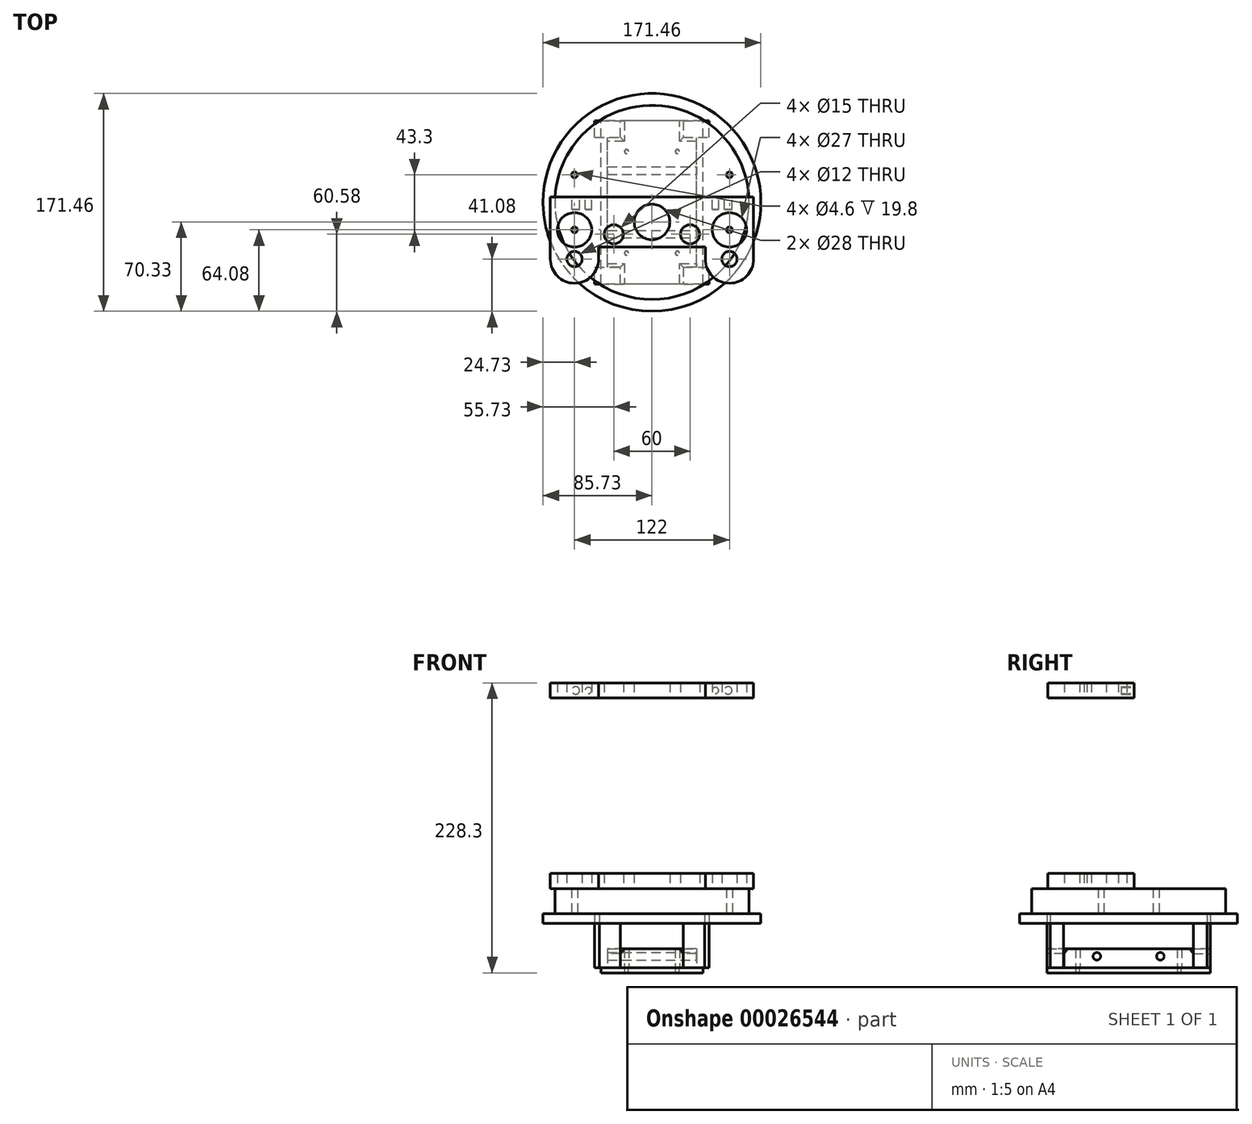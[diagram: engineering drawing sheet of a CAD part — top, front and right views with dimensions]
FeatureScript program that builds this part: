
annotation { "Feature Type Name" : "Feature", "Feature Type Description" : "" }
export const myFeature = defineFeature(function(context is Context, id is Id, definition is map)
    precondition{}
    {
        {
            var Q0;
            Q0=qCreatedBy(makeId("Top.planeOp"),FACE);
            var sketch = newSketch(context, id + "F0", { "sketchPlane" : qUnion([Q0])});
            skCircle(sketch, "E0", {"center": v(0, 0) * mm, "radius": 76.41 * mm});
            skCircle(sketch, "E1", {"center": v(-61, 21.65) * mm, "radius": 2.3 * mm});
            skCircle(sketch, "E2.0.1.0", {"center": v(-61, -21.65) * mm, "radius": 2.3 * mm});
            skCircle(sketch, "E2.1.0.0", {"center": v(61, 21.65) * mm, "radius": 2.3 * mm});
            skCircle(sketch, "E2.1.1.0", {"center": v(61, -21.65) * mm, "radius": 2.3 * mm});
            skLineSegment(sketch, "E2.direction2", {"start": v(-61, 21.65) * mm, "end": v(-61, -21.65) * mm, "construction": true});
            skSolve(sketch);
        }
        {
            var Q0;
            Q0=makeQuery(id+"F0.imprint","IMPRINT",FACE,{"disambiguationData":[TD([[makeQuery(id+"F0.imprint","IMPRINT",EDGE,{"derivedFrom":sQuery(id+"F0.wireOp",EDGE,"E0")}),1.0]])]});
            extrude(context, id + "F1", {"entities" : qUnion([Q0]), "depth" : 27.3 * mm});
        }
        {
            var Q0;
            Q0=makeQuery(id+"F1.opExtrude","CAP_FACE",FACE,{"disambiguationData":[OSD([sQuery(id+"F0.wireOp",EDGE,"E0"),sQuery(id+"F0.wireOp",EDGE,"E1"),sQuery(id+"F0.wireOp",EDGE,"E2.0.1.0"),sQuery(id+"F0.wireOp",EDGE,"E2.1.0.0"),sQuery(id+"F0.wireOp",EDGE,"E2.1.1.0")])],"isStart":true});
            var sketch = newSketch(context, id + "F2", { "sketchPlane" : qUnion([Q0])});
            skCircle(sketch, "E3", {"center": v(0, 0) * mm, "radius": 85.72 * mm});
            skLineSegment(sketch, "E4", {"start": v(0, 0) * mm, "end": v(0, 122.75) * mm, "construction": true});
            skLineSegment(sketch, "E5", {"start": v(0, 122.75) * mm, "end": v(0, -127.63) * mm, "construction": true});
            skLineSegment(sketch, "E6", {"start": v(0, 0) * mm, "end": v(-141.23, 0) * mm, "construction": true});
            skLineSegment(sketch, "E7", {"start": v(-141.23, 0) * mm, "end": v(142.28, 0) * mm, "construction": true});
            skLineSegment(sketch, "E8.0", {"start": v(-24.77, 64.25) * mm, "end": v(-24.77, 51.05) * mm});
            skLineSegment(sketch, "E9.0", {"start": v(24.76, 64.25) * mm, "end": v(24.76, 51.05) * mm});
            skLineSegment(sketch, "E10.0", {"start": v(45.08, 64.25) * mm, "end": v(45.08, 51.05) * mm});
            skLineSegment(sketch, "E11.0", {"start": v(-45.09, 64.25) * mm, "end": v(-45.09, 51.05) * mm});
            skLineSegment(sketch, "E12.0", {"start": v(-45.08, -51.05) * mm, "end": v(-24.76, -51.05) * mm});
            skLineSegment(sketch, "E13.0", {"start": v(-45.09, 51.05) * mm, "end": v(-24.77, 51.05) * mm});
            skLineSegment(sketch, "E14.0", {"start": v(-45.08, -64.25) * mm, "end": v(-24.76, -64.25) * mm});
            skLineSegment(sketch, "E15.0", {"start": v(-45.09, 64.25) * mm, "end": v(-24.77, 64.25) * mm});
            skLineSegment(sketch, "E16.trimOffspring", {"start": v(-45.09, -51.05) * mm, "end": v(-45.09, -64.25) * mm});
            skLineSegment(sketch, "E17.trimOffspring", {"start": v(-24.76, -51.05) * mm, "end": v(-24.76, -64.25) * mm});
            skLineSegment(sketch, "E18.trimOffspring", {"start": v(24.76, 51.05) * mm, "end": v(45.08, 51.05) * mm});
            skLineSegment(sketch, "E19.trimOffspring", {"start": v(24.76, 64.25) * mm, "end": v(45.08, 64.25) * mm});
            skLineSegment(sketch, "E20.trimOffspring", {"start": v(24.77, -51.05) * mm, "end": v(45.09, -51.05) * mm});
            skLineSegment(sketch, "E21.trimOffspring", {"start": v(24.77, -64.25) * mm, "end": v(45.09, -64.25) * mm});
            skLineSegment(sketch, "E22.trimOffspring", {"start": v(45.09, -51.05) * mm, "end": v(45.09, -64.25) * mm});
            skLineSegment(sketch, "E23.trimOffspring", {"start": v(24.77, -51.05) * mm, "end": v(24.77, -64.25) * mm});
            skSolve(sketch);
        }
        {
            var Q0;
            {var subQ5=sQuery(id+"F2.wireOp",EDGE,"E8.0");Q0=makeQuery(id+"F2.imprint","IMPRINT",FACE,{"disambiguationData":[TD([[makeQuery(id+"F2.imprint","IMPRINT",EDGE,{"derivedFrom":subQ5}),-1.0]])]});}
            var Q1;
            {var subQ5=sQuery(id+"F2.wireOp",EDGE,"E9.0");Q1=makeQuery(id+"F2.imprint","IMPRINT",FACE,{"disambiguationData":[TD([[makeQuery(id+"F2.imprint","IMPRINT",EDGE,{"derivedFrom":subQ5}),1.0]])]});}
            var Q2;
            {var subQ6=sQuery(id+"F2.wireOp",EDGE,"E20.trimOffspring");Q2=makeQuery(id+"F2.imprint","IMPRINT",FACE,{"disambiguationData":[TD([[makeQuery(id+"F2.imprint","IMPRINT",EDGE,{"derivedFrom":subQ6}),-1.0]])]});}
            var Q3;
            {var subQ6=sQuery(id+"F2.wireOp",EDGE,"E12.0");Q3=makeQuery(id+"F2.imprint","IMPRINT",FACE,{"disambiguationData":[TD([[makeQuery(id+"F2.imprint","IMPRINT",EDGE,{"derivedFrom":subQ6}),-1.0]])]});}
            extrude(context, id + "F3", {"entities" : qUnion([Q0, Q1, Q2, Q3]), "operationType" : NewBodyOperationType.ADD, "depth" : 35 * mm});
        }
        {
            var Q0;
            Q0 = qSketchRegion(id + "F2", true);
            extrude(context, id + "F4", {"entities" : qUnion([Q0]), "operationType" : NewBodyOperationType.ADD, "oppositeDirection" : true, "depth" : 7.5 * mm});
        }
        {
            var Q0;
            Q0=makeQuery(id+"F1.opExtrude","CAP_FACE",FACE,{"disambiguationData":[OSD([sQuery(id+"F0.wireOp",EDGE,"E0"),sQuery(id+"F0.wireOp",EDGE,"E1"),sQuery(id+"F0.wireOp",EDGE,"E2.0.1.0"),sQuery(id+"F0.wireOp",EDGE,"E2.1.0.0"),sQuery(id+"F0.wireOp",EDGE,"E2.1.1.0")])],"isStart":false});
            var sketch = newSketch(context, id + "F5", { "sketchPlane" : qUnion([Q0])});
            skCircle(sketch, "E24.0", {"center": v(-61, -21.65) * mm, "radius": 2.3 * mm});
            skCircle(sketch, "E25.0", {"center": v(61, -21.65) * mm, "radius": 2.3 * mm});
            skLineSegment(sketch, "E26", {"start": v(-80, -21.65) * mm, "end": v(80, -21.65) * mm, "construction": true});
            skCircle(sketch, "E27", {"center": v(-61, -21.65) * mm, "radius": 13.5 * mm});
            skCircle(sketch, "E28", {"center": v(61, -21.65) * mm, "radius": 13.5 * mm});
            skLineSegment(sketch, "E29", {"start": v(61, 4.35) * mm, "end": v(61, -57.65) * mm, "construction": true});
            skLineSegment(sketch, "E30", {"start": v(-61, 4.35) * mm, "end": v(-61, -57.65) * mm, "construction": true});
            skCircle(sketch, "E31", {"center": v(61, -44.65) * mm, "radius": 6 * mm});
            skCircle(sketch, "E32", {"center": v(-61, -44.65) * mm, "radius": 6 * mm});
            skLineSegment(sketch, "E33.0", {"start": v(80, 4.35) * mm, "end": v(80, -44.65) * mm});
            skLineSegment(sketch, "E34", {"start": v(-42, -44.65) * mm, "end": v(-42, -35.15) * mm});
            skLineSegment(sketch, "E35.MirrorCS", {"start": v(42, -44.65) * mm, "end": v(42, -35.15) * mm});
            skLineSegment(sketch, "E36.trimOffspring", {"start": v(-42, -35.15) * mm, "end": v(42, -35.15) * mm});
            skPoint(sketch, "E37.orphan", {"position": v(-42, -21.65) * mm});
            skPoint(sketch, "E38.orphan", {"position": v(42, -21.65) * mm});
            skArc(sketch, "E39", {"start": v(-80, -44.65) * mm, "mid": v(-61, -63.65) * mm, "end": v(-42, -44.65) * mm});
            skArc(sketch, "E40", {"start": v(42, -44.65) * mm, "mid": v(61, -63.65) * mm, "end": v(80, -44.65) * mm});
            skPoint(sketch, "E41.orphan", {"position": v(80, -57.65) * mm});
            skLineSegment(sketch, "E42", {"start": v(0, 4.35) * mm, "end": v(0, -35.15) * mm, "construction": true});
            skPoint(sketch, "E43.orphan", {"position": v(0, -15.4) * mm});
            skLineSegment(sketch, "E44.0", {"start": v(-30, -15.15) * mm, "end": v(-30, -35.15) * mm, "construction": true});
            skLineSegment(sketch, "E45.0", {"start": v(30, -15.15) * mm, "end": v(30, -35.15) * mm, "construction": true});
            skCircle(sketch, "E46", {"center": v(-30, -25.15) * mm, "radius": 7.5 * mm});
            skCircle(sketch, "E47", {"center": v(30, -25.15) * mm, "radius": 7.5 * mm});
            skLineSegment(sketch, "E48", {"start": v(-80, -44.65) * mm, "end": v(-80, 4.35) * mm});
            skLineSegment(sketch, "E49", {"start": v(80, 4.35) * mm, "end": v(-80, 4.35) * mm});
            skCircle(sketch, "E50", {"center": v(0, -15.4) * mm, "radius": 14 * mm});
            skSolve(sketch);
        }
        {
            var Q0;
            Q0 = qSketchRegion(id + "F5", true);
            extrude(context, id + "F6", {"entities" : qUnion([Q0]), "depth" : 12 * mm});
        }
        {
            var Q0;
            Q0=makeQuery(id+"F6.opExtrude","SWEPT_BODY",BODY,{"disambiguationData":[OSD([sQuery(id+"F5.wireOp",EDGE,"E27"),sQuery(id+"F5.wireOp",EDGE,"E28"),sQuery(id+"F5.wireOp",EDGE,"E31"),sQuery(id+"F5.wireOp",EDGE,"E32"),sQuery(id+"F5.wireOp",EDGE,"E33.0"),sQuery(id+"F5.wireOp",EDGE,"E34"),sQuery(id+"F5.wireOp",EDGE,"E35.MirrorCS"),sQuery(id+"F5.wireOp",EDGE,"E36.trimOffspring"),sQuery(id+"F5.wireOp",EDGE,"E39"),sQuery(id+"F5.wireOp",EDGE,"E40"),sQuery(id+"F5.wireOp",EDGE,"E46"),sQuery(id+"F5.wireOp",EDGE,"E47"),sQuery(id+"F5.wireOp",EDGE,"E48"),sQuery(id+"F5.wireOp",EDGE,"E49")])]});
            transform(context, id + "F7", {"entities" : qUnion([Q0]), "transformType" : TransformType.TRANSLATION_3D, "dx" : 0 * mm, "dy" : 0 * mm, "dz" : 150 * mm, "makeCopy" : true});
        }
        {
            var Q0;
            Q0=makeQuery(id+"F3.opExtrude","CAP_FACE",FACE,{"disambiguationData":[OSD([sQuery(id+"F0.wireOp",EDGE,"E0"),sQuery(id+"F2.wireOp",EDGE,"E20.trimOffspring"),sQuery(id+"F2.wireOp",EDGE,"E21.trimOffspring"),sQuery(id+"F2.wireOp",EDGE,"E22.trimOffspring"),sQuery(id+"F2.wireOp",EDGE,"E23.trimOffspring")])],"isStart":false});
            var sketch = newSketch(context, id + "F8", { "sketchPlane" : qUnion([Q0])});
            skLineSegment(sketch, "E51.0", {"start": v(-35.09, 51.05) * mm, "end": v(-35.09, -51.05) * mm});
            skLineSegment(sketch, "E52", {"start": v(0, 64.25) * mm, "end": v(0, -64.25) * mm, "construction": true});
            skCircle(sketch, "E53", {"center": v(20, 40) * mm, "radius": 1.65 * mm});
            skCircle(sketch, "E54", {"center": v(-20, 40) * mm, "radius": 1.65 * mm});
            skCircle(sketch, "E55", {"center": v(-20, -40) * mm, "radius": 1.65 * mm});
            skCircle(sketch, "E56", {"center": v(20, -40) * mm, "radius": 1.65 * mm});
            skPoint(sketch, "E57", {"position": v(45.09, -51.05) * mm});
            skLineSegment(sketch, "E58.top", {"start": v(24.77, -64.25) * mm, "end": v(-24.77, -64.25) * mm});
            skLineSegment(sketch, "E59", {"start": v(-35.08, 0) * mm, "end": v(33.13, 0) * mm, "construction": true});
            skPoint(sketch, "E60.MirrorP", {"position": v(45.09, 51.05) * mm});
            skLineSegment(sketch, "E61.MirrorCS", {"start": v(35.09, 51.05) * mm, "end": v(35.09, -51.05) * mm});
            skLineSegment(sketch, "E62", {"start": v(35.09, -51.03) * mm, "end": v(24.77, -51.05) * mm});
            skLineSegment(sketch, "E63", {"start": v(24.77, -51.05) * mm, "end": v(24.77, -64.25) * mm});
            skPoint(sketch, "E64.orphan", {"position": v(45.09, -64.25) * mm});
            skLineSegment(sketch, "E65.MirrorCS", {"start": v(-35.09, -51.03) * mm, "end": v(-24.77, -51.05) * mm});
            skLineSegment(sketch, "E66.MirrorCS", {"start": v(-24.77, -51.05) * mm, "end": v(-24.77, -64.25) * mm});
            skPoint(sketch, "E67.orphan", {"position": v(-45.09, -64.25) * mm});
            skPoint(sketch, "E68.orphan", {"position": v(-45.09, 64.25) * mm});
            skPoint(sketch, "E69.MirrorCS.start.orphan", {"position": v(45.09, 64.25) * mm});
            skLineSegment(sketch, "E70.MirrorCS", {"start": v(24.77, 64.25) * mm, "end": v(-24.77, 64.25) * mm});
            skLineSegment(sketch, "E71.MirrorCS", {"start": v(24.77, 51.05) * mm, "end": v(24.77, 64.25) * mm});
            skLineSegment(sketch, "E72.MirrorCS", {"start": v(35.08, 51.03) * mm, "end": v(24.76, 51.05) * mm});
            skLineSegment(sketch, "E73.MirrorCS", {"start": v(-24.77, 51.05) * mm, "end": v(-24.77, 64.25) * mm});
            skLineSegment(sketch, "E74.MirrorCS", {"start": v(-35.08, 51.03) * mm, "end": v(-24.76, 51.05) * mm});
            skSolve(sketch);
        }
        {
            var Q0;
            Q0=makeQuery(id+"F8.imprint","IMPRINT",FACE,{"disambiguationData":[TD([[makeQuery(id+"F8.imprint","IMPRINT",EDGE,{"derivedFrom":sQuery(id+"F8.wireOp",EDGE,"E51.0")}),1.0]])]});
            var Q1;
            {var subQ3=makeQuery(id+"F3.opExtrude","CAP_EDGE",EDGE,{"disambiguationData":[OSD([sQuery(id+"F2.wireOp",EDGE,"E23.trimOffspring")])],"isStart":false});Q1=makeQuery(id+"F8.imprint","IMPRINT",FACE,{"disambiguationData":[TD([[makeQuery(id+"F8.imprint","IMPRINT",EDGE,{"derivedFrom":subQ3}),1.0]])]});}
            extrude(context, id + "F9", {"entities" : qUnion([Q0, Q1]), "oppositeDirection" : true, "depth" : 15 * mm});
        }
        {
            var Q0;
            Q0=makeQuery(id+"F9.opExtrude","CAP_FACE",FACE,{"disambiguationData":[OSD([sQuery(id+"F8.wireOp",EDGE,"7d342810-ca8f-4171-a29e-d5170556719c.bottom"),sQuery(id+"F8.wireOp",EDGE,"7d342810-ca8f-4171-a29e-d5170556719c.top"),sQuery(id+"F8.wireOp",EDGE,"045c881f-2920-4f37-9ffd-bd33b600ad80"),sQuery(id+"F8.wireOp",EDGE,"67255690-9789-45ab-b37c-ab91037836ce"),sQuery(id+"F8.wireOp",EDGE,"bf8d3838-71e3-4a16-8931-b95f2f1fb24f"),sQuery(id+"F8.wireOp",EDGE,"6194312e-fd42-43f2-88cc-18e898c91ba5"),sQuery(id+"F8.wireOp",EDGE,"87c38c34-f4bd-43af-876b-18c21d3a21c2"),sQuery(id+"F8.wireOp",EDGE,"f36fb309-0f78-4d31-8950-d358daa3116d"),sQuery(id+"F8.wireOp",EDGE,"0a54a875-1903-4d55-a390-c70b188df6e4"),sQuery(id+"F8.wireOp",EDGE,"1168e47b-7984-4174-9ad8-cdda6da24c65"),sQuery(id+"F8.wireOp",EDGE,"59441c3e-5a51-4e7b-9414-e97e827ee6d7.0"),sQuery(id+"F8.wireOp",EDGE,"E51.0")])],"isStart":true});
            var sketch = newSketch(context, id + "F10", { "sketchPlane" : qUnion([Q0])});
            skPoint(sketch, "E75.orphan", {"position": v(24.77, 64.25) * mm});
            skPoint(sketch, "E76.orphan", {"position": v(-24.77, 64.25) * mm});
            skPoint(sketch, "E77.orphan", {"position": v(-35.09, -51.03) * mm});
            skPoint(sketch, "E78.orphan", {"position": v(-24.77, -64.25) * mm});
            skPoint(sketch, "E79.orphan", {"position": v(24.77, -64.25) * mm});
            skLineSegment(sketch, "E80.bottom", {"start": v(40.08, 64.25) * mm, "end": v(-40.08, 64.25) * mm});
            skLineSegment(sketch, "E80.top", {"start": v(40.08, -64.25) * mm, "end": v(-40.08, -64.25) * mm});
            skPoint(sketch, "E81.endSnap0", {"position": v(35.08, 0) * mm});
            skLineSegment(sketch, "E82", {"start": v(0, 64.25) * mm, "end": v(0, -101.25) * mm, "construction": true});
            skPoint(sketch, "E83", {"position": v(20, 40) * mm});
            skPoint(sketch, "E84", {"position": v(-20, 40) * mm});
            skPoint(sketch, "E85", {"position": v(-20, -40) * mm});
            skPoint(sketch, "E86", {"position": v(20, -40) * mm});
            skCircle(sketch, "E87", {"center": v(-20, 40) * mm, "radius": 1.5 * mm});
            skCircle(sketch, "E88", {"center": v(-20, -40) * mm, "radius": 1.5 * mm});
            skCircle(sketch, "E89", {"center": v(20, 40) * mm, "radius": 1.5 * mm});
            skCircle(sketch, "E90", {"center": v(20, -40) * mm, "radius": 1.5 * mm});
            skLineSegment(sketch, "E91.0", {"start": v(40.08, 64.25) * mm, "end": v(40.08, -64.25) * mm});
            skLineSegment(sketch, "E92.0", {"start": v(-40.08, 64.25) * mm, "end": v(-40.08, -64.25) * mm});
            skSolve(sketch);
        }
        {
            var Q0;
            Q0 = qSketchRegion(id + "F10", true);
            extrude(context, id + "F11", {"entities" : qUnion([Q0]), "depth" : 4 * mm});
        }
        {
            var Q0;
            Q0=makeQuery(id+"F9.opExtrude","CAP_EDGE",EDGE,{"disambiguationData":[OSD([sQuery(id+"F8.wireOp",EDGE,"E66.MirrorCS")])],"isStart":false});
            var Q1;
            Q1=makeQuery(id+"F9.opExtrude","CAP_EDGE",EDGE,{"disambiguationData":[OSD([sQuery(id+"F8.wireOp",EDGE,"E65.MirrorCS")])],"isStart":false});
            var Q2;
            Q2=makeQuery(id+"F9.opExtrude","CAP_EDGE",EDGE,{"disambiguationData":[OSD([sQuery(id+"F8.wireOp",EDGE,"E63")])],"isStart":false});
            var Q3;
            Q3=makeQuery(id+"F9.opExtrude","CAP_EDGE",EDGE,{"disambiguationData":[OSD([sQuery(id+"F8.wireOp",EDGE,"E62")])],"isStart":false});
            var Q4;
            Q4=makeQuery(id+"F9.opExtrude","CAP_EDGE",EDGE,{"disambiguationData":[OSD([sQuery(id+"F8.wireOp",EDGE,"E72.MirrorCS")])],"isStart":false});
            var Q5;
            Q5=makeQuery(id+"F9.opExtrude","CAP_EDGE",EDGE,{"disambiguationData":[OSD([sQuery(id+"F8.wireOp",EDGE,"E71.MirrorCS")])],"isStart":false});
            var Q6;
            Q6=makeQuery(id+"F9.opExtrude","CAP_EDGE",EDGE,{"disambiguationData":[OSD([sQuery(id+"F8.wireOp",EDGE,"E73.MirrorCS")])],"isStart":false});
            var Q7;
            Q7=makeQuery(id+"F9.opExtrude","CAP_EDGE",EDGE,{"disambiguationData":[OSD([sQuery(id+"F8.wireOp",EDGE,"E74.MirrorCS")])],"isStart":false});
            chamfer(context, id + "F12", {"entities" : qUnion([Q0, Q1, Q2, Q3, Q4, Q5, Q6, Q7]), "chamferType" : ChamferType.TWO_OFFSETS, "width1" : 4 * mm, "oppositeDirection" : false, "width2" : 3 * mm, "tangentPropagation" : true});
        }
        {
            var Q0;
            Q0=makeQuery(id+"F7.opPattern","COPY",FACE,{"derivedFrom":makeQuery(id+"F6.opExtrude","SWEPT_FACE",FACE,{"disambiguationData":[OSD([sQuery(id+"F5.wireOp",EDGE,"E49")])]}),"instanceName":"1"});
            var sketch = newSketch(context, id + "F13", { "sketchPlane" : qUnion([Q0])});
            skCircle(sketch, "E93", {"center": v(-60, 183.3) * mm, "radius": 3 * mm});
            skCircle(sketch, "E94", {"center": v(-50, 183.3) * mm, "radius": 2.5 * mm});
            skCircle(sketch, "E95", {"center": v(50, 183.3) * mm, "radius": 2.5 * mm});
            skCircle(sketch, "E96", {"center": v(60, 183.3) * mm, "radius": 3 * mm});
            skPoint(sketch, "E97", {"position": v(0, 177.3) * mm});
            skSolve(sketch);
        }
        {
            var Q0;
            Q0=makeQuery(id+"F13.imprint","IMPRINT",FACE,{"disambiguationData":[TD([[makeQuery(id+"F13.imprint","IMPRINT",EDGE,{"derivedFrom":sQuery(id+"F13.wireOp",EDGE,"E93")}),1.0]])]});
            var Q1;
            Q1=makeQuery(id+"F13.imprint","IMPRINT",FACE,{"disambiguationData":[TD([[makeQuery(id+"F13.imprint","IMPRINT",EDGE,{"derivedFrom":sQuery(id+"F13.wireOp",EDGE,"E94")}),1.0]])]});
            var Q2;
            Q2=makeQuery(id+"F13.imprint","IMPRINT",FACE,{"disambiguationData":[TD([[makeQuery(id+"F13.imprint","IMPRINT",EDGE,{"derivedFrom":sQuery(id+"F13.wireOp",EDGE,"E95")}),1.0]])]});
            var Q3;
            Q3=makeQuery(id+"F13.imprint","IMPRINT",FACE,{"disambiguationData":[TD([[makeQuery(id+"F13.imprint","IMPRINT",EDGE,{"derivedFrom":sQuery(id+"F13.wireOp",EDGE,"E96")}),1.0]])]});
            extrude(context, id + "F14", {"entities" : qUnion([Q0, Q1, Q2, Q3]), "operationType" : NewBodyOperationType.REMOVE, "oppositeDirection" : true, "depth" : 10 * mm});
        }
        {
            var Q0;
            Q0=makeQuery(id+"F9.opExtrude","SWEPT_FACE",FACE,{"disambiguationData":[OSD([sQuery(id+"F8.wireOp",EDGE,"E61.MirrorCS")])]});
            var sketch = newSketch(context, id + "F15", { "sketchPlane" : qUnion([Q0])});
            skLineSegment(sketch, "E98", {"start": v(0, -35) * mm, "end": v(0, 42.28) * mm, "construction": true});
            skPoint(sketch, "E98.endSnap0", {"position": v(0, -35) * mm});
            skPoint(sketch, "E99", {"position": v(25, -26) * mm});
            skPoint(sketch, "E100", {"position": v(-25, -26) * mm});
            skSolve(sketch);
        }
        {
            var Q0;
            Q0=sQuery(id+"F15.wireOp",VERTEX,"E99");
            var Q1;
            Q1=sQuery(id+"F15.wireOp",VERTEX,"E100");
            var Q2;
            Q2=makeQuery(id+"F9.opExtrude","SWEPT_BODY",BODY,{"disambiguationData":[OSD([sQuery(id+"F8.wireOp",EDGE,"E51.0"),sQuery(id+"F8.wireOp",EDGE,"E53"),sQuery(id+"F8.wireOp",EDGE,"E54"),sQuery(id+"F8.wireOp",EDGE,"E55"),sQuery(id+"F8.wireOp",EDGE,"E56"),sQuery(id+"F8.wireOp",EDGE,"E58.top"),sQuery(id+"F8.wireOp",EDGE,"E61.MirrorCS"),sQuery(id+"F8.wireOp",EDGE,"E62"),sQuery(id+"F8.wireOp",EDGE,"E63"),sQuery(id+"F8.wireOp",EDGE,"E65.MirrorCS"),sQuery(id+"F8.wireOp",EDGE,"E66.MirrorCS"),sQuery(id+"F8.wireOp",EDGE,"E70.MirrorCS"),sQuery(id+"F8.wireOp",EDGE,"E71.MirrorCS"),sQuery(id+"F8.wireOp",EDGE,"E72.MirrorCS"),sQuery(id+"F8.wireOp",EDGE,"E73.MirrorCS"),sQuery(id+"F8.wireOp",EDGE,"E74.MirrorCS")])]});
            hole(context, id + "F16", {"style" : HoleStyle.SIMPLE, "endStyle" : HoleEndStyle.THROUGH, "holeDiameter" : 6 * mm, "locations" : qUnion([Q0, Q1]), "scope" : qUnion([Q2]), "isTappedThrough" : true});
        }
    });
